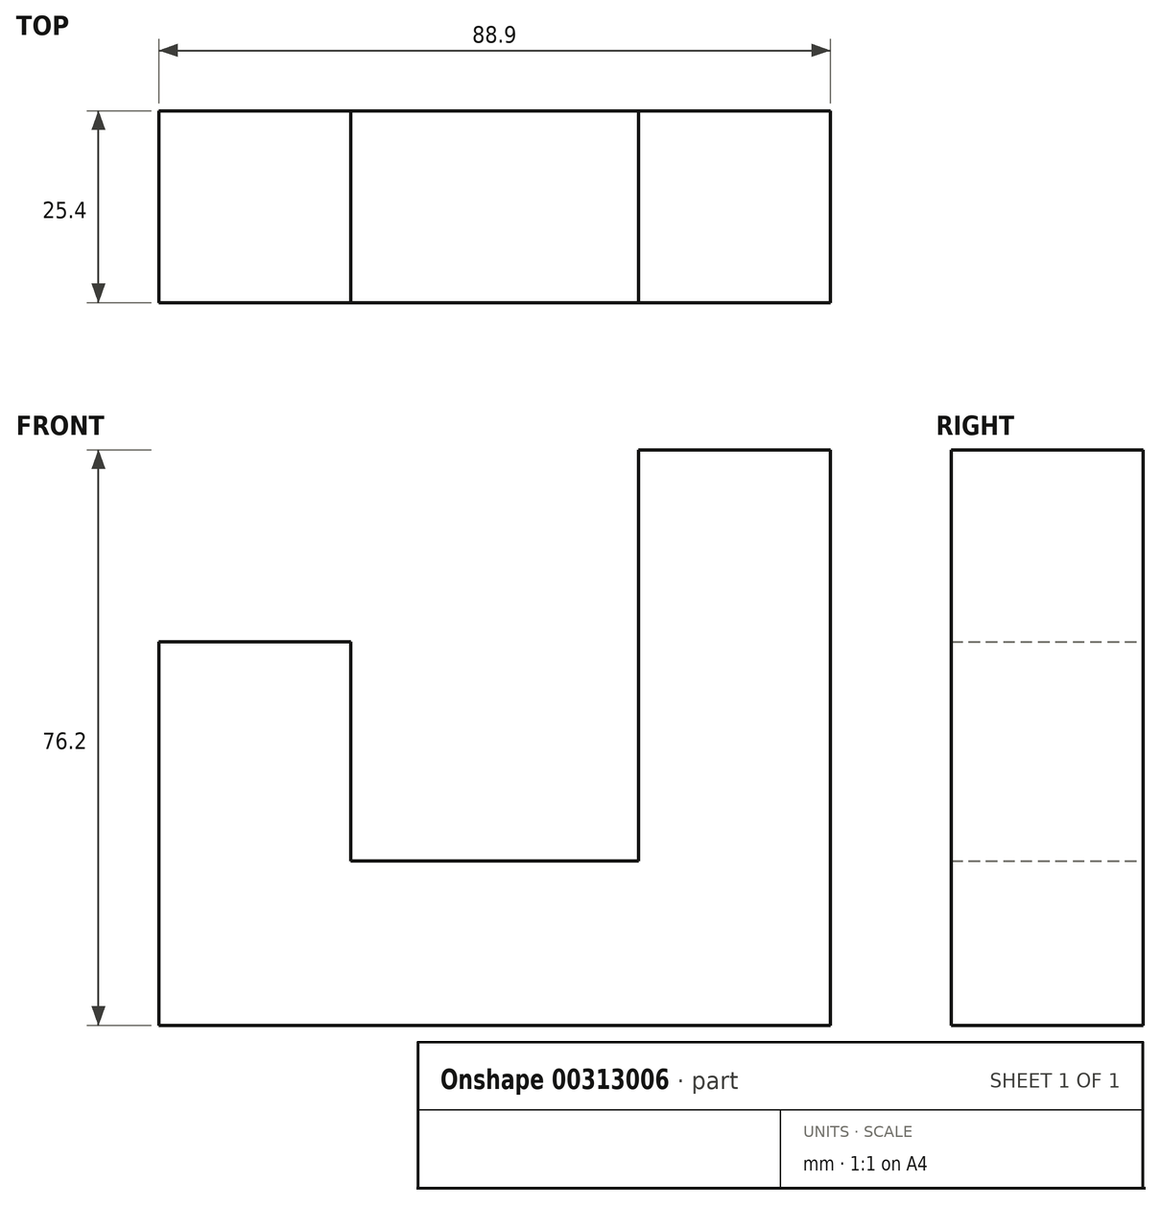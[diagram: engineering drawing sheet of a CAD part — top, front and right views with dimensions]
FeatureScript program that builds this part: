
annotation { "Feature Type Name" : "Feature", "Feature Type Description" : "" }
export const myFeature = defineFeature(function(context is Context, id is Id, definition is map)
    precondition{}
    {
        {
            var Q0;
            Q0=qCreatedBy(makeId("Front.planeOp"),FACE);
            var sketch = newSketch(context, id + "F0", { "sketchPlane" : qUnion([Q0])});
            skLineSegment(sketch, "E0", {"start": v(-79.37, -30.7) * mm, "end": v(-53.97, -30.7) * mm});
            skLineSegment(sketch, "E1", {"start": v(-53.97, -30.7) * mm, "end": v(-53.97, -59.75) * mm});
            skLineSegment(sketch, "E2", {"start": v(-53.97, -59.75) * mm, "end": v(-15.87, -59.75) * mm});
            skLineSegment(sketch, "E3", {"start": v(-15.87, -59.75) * mm, "end": v(-15.87, -5.3) * mm});
            skLineSegment(sketch, "E4", {"start": v(-15.87, -5.3) * mm, "end": v(9.53, -5.3) * mm});
            skLineSegment(sketch, "E5", {"start": v(9.53, -5.3) * mm, "end": v(9.53, -81.5) * mm});
            skLineSegment(sketch, "E6", {"start": v(9.53, -81.5) * mm, "end": v(-79.37, -81.5) * mm});
            skLineSegment(sketch, "E7", {"start": v(-79.37, -81.5) * mm, "end": v(-79.37, -30.7) * mm});
            skSolve(sketch);
        }
        {
            var Q0;
            Q0=makeQuery(id+"F0.imprint","IMPRINT",FACE,{"disambiguationData":[TD([[makeQuery(id+"F0.imprint","IMPRINT",EDGE,{"derivedFrom":sQuery(id+"F0.wireOp",EDGE,"E0")}),-1.0]])]});
            extrude(context, id + "F1", {"entities" : qUnion([Q0]), "depth" : 25.4 * mm});
        }
    });
